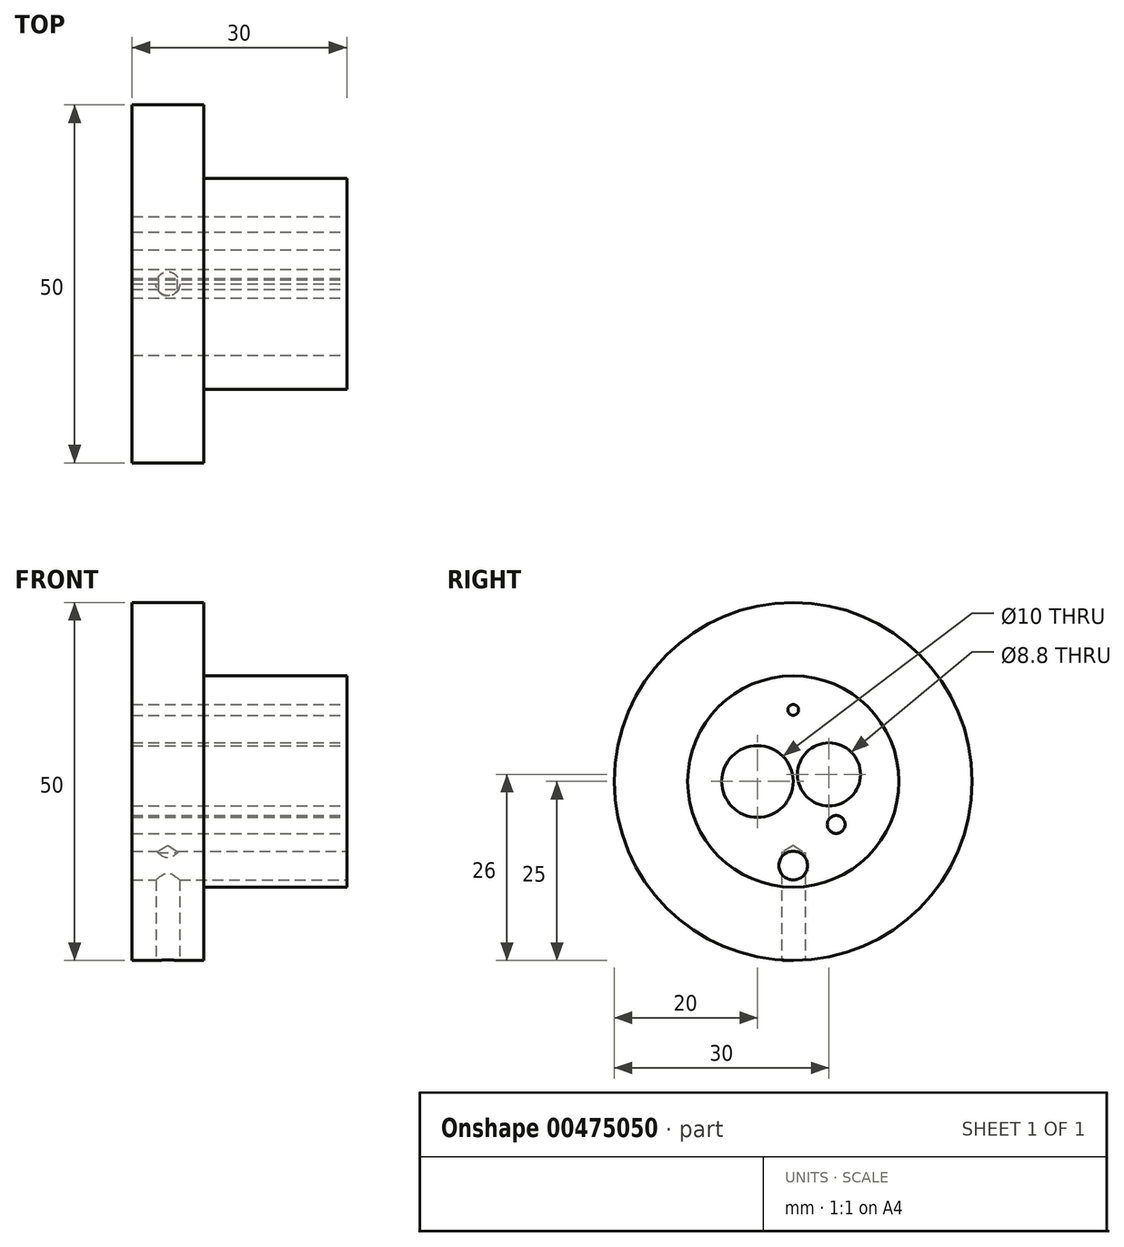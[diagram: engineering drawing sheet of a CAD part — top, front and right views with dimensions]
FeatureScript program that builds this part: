
annotation { "Feature Type Name" : "Feature", "Feature Type Description" : "" }
export const myFeature = defineFeature(function(context is Context, id is Id, definition is map)
    precondition{}
    {
        {
            var Q0;
            Q0=qCreatedBy(makeId("Front.planeOp"),FACE);
            var sketch = newSketch(context, id + "F0", { "sketchPlane" : qUnion([Q0])});
            skLineSegment(sketch, "E0", {"start": v(-37.74, 0) * mm, "end": v(42.42, 0) * mm, "construction": true});
            skLineSegment(sketch, "E1", {"start": v(-10, 0) * mm, "end": v(-10, 25) * mm});
            skLineSegment(sketch, "E2", {"start": v(-10, 25) * mm, "end": v(0, 25) * mm});
            skLineSegment(sketch, "E3", {"start": v(0, 25) * mm, "end": v(0, 14.75) * mm});
            skLineSegment(sketch, "E4", {"start": v(0, 14.75) * mm, "end": v(20, 14.75) * mm});
            skLineSegment(sketch, "E5", {"start": v(20, 14.75) * mm, "end": v(20, 0) * mm});
            skLineSegment(sketch, "E6", {"start": v(20, 0) * mm, "end": v(-10, 0) * mm});
            skSolve(sketch);
        }
        {
            var Q0;
            Q0=makeQuery(id+"F0.imprint","IMPRINT",FACE,{"disambiguationData":[TD([[makeQuery(id+"F0.imprint","IMPRINT",EDGE,{"derivedFrom":sQuery(id+"F0.wireOp",EDGE,"E1")}),-1.0]])]});
            var Q1;
            Q1=sQuery(id+"F0.wireOp",EDGE,"E6");
            revolve(context, id + "F1", {"entities" : qUnion([Q0]), "axis" : qUnion([Q1]), "revolveType" : RevolveType.FULL});
        }
        {
            var Q0;
            Q0=makeQuery(id+"F1.opRevolve","SWEPT_FACE",FACE,{"disambiguationData":[OSD([sQuery(id+"F0.wireOp",EDGE,"E5")])]});
            var sketch = newSketch(context, id + "F2", { "sketchPlane" : qUnion([Q0])});
            skPoint(sketch, "E7", {"position": v(0, -11.75) * mm});
            skSolve(sketch);
        }
        {
            var Q0;
            Q0=sQuery(id+"F2.wireOp",VERTEX,"E7");
            var Q1;
            Q1=makeQuery(id+"F1.opRevolve","SWEPT_BODY",BODY,{"disambiguationData":[OSD([sQuery(id+"F0.wireOp",EDGE,"E1"),sQuery(id+"F0.wireOp",EDGE,"E2"),sQuery(id+"F0.wireOp",EDGE,"E3"),sQuery(id+"F0.wireOp",EDGE,"E4"),sQuery(id+"F0.wireOp",EDGE,"E5"),sQuery(id+"F0.wireOp",EDGE,"E6")])]});
            hole(context, id + "F3", {"style" : HoleStyle.SIMPLE, "endStyle" : HoleEndStyle.THROUGH, "holeDiameter" : 4 * mm, "isTappedThrough" : true, "tappedDepth" : 5 * mm, "tapClearance" : 2, "locations" : qUnion([Q0]), "scope" : qUnion([Q1])});
        }
        {
            var Q0;
            Q0=qCreatedBy(makeId("Top.planeOp"),FACE);
            cPlane(context, id + "F4", {"entities" : qUnion([Q0]), "cplaneType" : CPlaneType.OFFSET, "offset" : 25 * mm, "oppositeDirection" : true, "width" : 150 * mm, "height" : 150 * mm});
        }
        {
            var Q0;
            Q0=qCreatedBy(id+"F4.planeOp",FACE);
            var sketch = newSketch(context, id + "F5", { "sketchPlane" : qUnion([Q0])});
            skPoint(sketch, "E8", {"position": v(-5, 0) * mm});
            skSolve(sketch);
        }
        {
            var Q0;
            Q0=sQuery(id+"F5.wireOp",VERTEX,"E8");
            var Q1;
            Q1=makeQuery(id+"F1.opRevolve","SWEPT_BODY",BODY,{"disambiguationData":[OSD([sQuery(id+"F0.wireOp",EDGE,"E1"),sQuery(id+"F0.wireOp",EDGE,"E2"),sQuery(id+"F0.wireOp",EDGE,"E3"),sQuery(id+"F0.wireOp",EDGE,"E4"),sQuery(id+"F0.wireOp",EDGE,"E5"),sQuery(id+"F0.wireOp",EDGE,"E6")])]});
            hole(context, id + "F6", {"style" : HoleStyle.SIMPLE, "endStyle" : HoleEndStyle.BLIND, "oppositeDirection" : true, "standardTappedOrClearance" : lookupTablePath({ "standard" : "ISO", "engagement" : "75%", "pitch" : "0.7 mm", "size" : "M4", "type" : "Tapped" }), "standardBlindInLast" : lookupTablePath({ "standard" : "ISO", "engagement" : "75%", "pitch" : "0.7 mm", "size" : "M4", "type" : "Tapped" }), "holeDiameter" : 3.3 * mm, "showTappedDepth" : true, "holeDepth" : 15 * mm, "isTappedThrough" : true, "tappedDepth" : 13.6 * mm, "tapClearance" : 2, "locations" : qUnion([Q0]), "scope" : qUnion([Q1]), "majorDiameter" : 4 * mm});
        }
        {
            var Q0;
            Q0=makeQuery(id+"F1.opRevolve","SWEPT_FACE",FACE,{"disambiguationData":[OSD([sQuery(id+"F0.wireOp",EDGE,"E5")])]});
            var sketch = newSketch(context, id + "F7", { "sketchPlane" : qUnion([Q0])});
            skPoint(sketch, "E9", {"position": v(-5, 0) * mm});
            skPoint(sketch, "E10", {"position": v(5, 1) * mm});
            skPoint(sketch, "E11", {"position": v(6, -6) * mm});
            skPoint(sketch, "E12", {"position": v(0, 10) * mm});
            skSolve(sketch);
        }
        {
            var Q0;
            Q0=sQuery(id+"F7.wireOp",VERTEX,"E9");
            var Q1;
            Q1=makeQuery(id+"F1.opRevolve","SWEPT_BODY",BODY,{"disambiguationData":[OSD([sQuery(id+"F0.wireOp",EDGE,"E1"),sQuery(id+"F0.wireOp",EDGE,"E2"),sQuery(id+"F0.wireOp",EDGE,"E3"),sQuery(id+"F0.wireOp",EDGE,"E4"),sQuery(id+"F0.wireOp",EDGE,"E5"),sQuery(id+"F0.wireOp",EDGE,"E6")])]});
            hole(context, id + "F8", {"style" : HoleStyle.SIMPLE, "endStyle" : HoleEndStyle.THROUGH, "holeDiameter" : 10 * mm, "isTappedThrough" : true, "tappedDepth" : 13.6 * mm, "tapClearance" : 2, "locations" : qUnion([Q0]), "scope" : qUnion([Q1])});
        }
        {
            var Q0;
            Q0=sQuery(id+"F7.wireOp",VERTEX,"E10");
            var Q1;
            Q1=makeQuery(id+"F1.opRevolve","SWEPT_BODY",BODY,{"disambiguationData":[OSD([sQuery(id+"F0.wireOp",EDGE,"E1"),sQuery(id+"F0.wireOp",EDGE,"E2"),sQuery(id+"F0.wireOp",EDGE,"E3"),sQuery(id+"F0.wireOp",EDGE,"E4"),sQuery(id+"F0.wireOp",EDGE,"E5"),sQuery(id+"F0.wireOp",EDGE,"E6")])]});
            hole(context, id + "F9", {"style" : HoleStyle.SIMPLE, "endStyle" : HoleEndStyle.THROUGH, "standardTappedOrClearance" : lookupTablePath({ "standard" : "ISO", "engagement" : "75%", "pitch" : "1.25 mm", "size" : "M10", "type" : "Tapped" }), "standardBlindInLast" : lookupTablePath({ "standard" : "ISO", "engagement" : "75%", "pitch" : "1.25 mm", "size" : "M10", "type" : "Tapped" }), "holeDiameter" : 8.8 * mm, "showTappedDepth" : true, "isTappedThrough" : true, "tappedDepth" : 13.6 * mm, "tapClearance" : 2, "locations" : qUnion([Q0]), "scope" : qUnion([Q1]), "majorDiameter" : 10 * mm});
        }
        {
            var Q0;
            Q0=sQuery(id+"F7.wireOp",VERTEX,"E12");
            var Q1;
            Q1=makeQuery(id+"F1.opRevolve","SWEPT_BODY",BODY,{"disambiguationData":[OSD([sQuery(id+"F0.wireOp",EDGE,"E1"),sQuery(id+"F0.wireOp",EDGE,"E2"),sQuery(id+"F0.wireOp",EDGE,"E3"),sQuery(id+"F0.wireOp",EDGE,"E4"),sQuery(id+"F0.wireOp",EDGE,"E5"),sQuery(id+"F0.wireOp",EDGE,"E6")])]});
            hole(context, id + "F10", {"style" : HoleStyle.SIMPLE, "endStyle" : HoleEndStyle.THROUGH, "holeDiameter" : 1.5 * mm, "isTappedThrough" : true, "tappedDepth" : 13.6 * mm, "tapClearance" : 2, "locations" : qUnion([Q0]), "scope" : qUnion([Q1])});
        }
        {
            var Q0;
            Q0=sQuery(id+"F7.wireOp",VERTEX,"E11");
            var Q1;
            Q1=makeQuery(id+"F1.opRevolve","SWEPT_BODY",BODY,{"disambiguationData":[OSD([sQuery(id+"F0.wireOp",EDGE,"E1"),sQuery(id+"F0.wireOp",EDGE,"E2"),sQuery(id+"F0.wireOp",EDGE,"E3"),sQuery(id+"F0.wireOp",EDGE,"E4"),sQuery(id+"F0.wireOp",EDGE,"E5"),sQuery(id+"F0.wireOp",EDGE,"E6")])]});
            hole(context, id + "F11", {"style" : HoleStyle.SIMPLE, "endStyle" : HoleEndStyle.THROUGH, "holeDiameter" : 2.5 * mm, "isTappedThrough" : true, "tappedDepth" : 13.6 * mm, "tapClearance" : 2, "locations" : qUnion([Q0]), "scope" : qUnion([Q1])});
        }
    });
